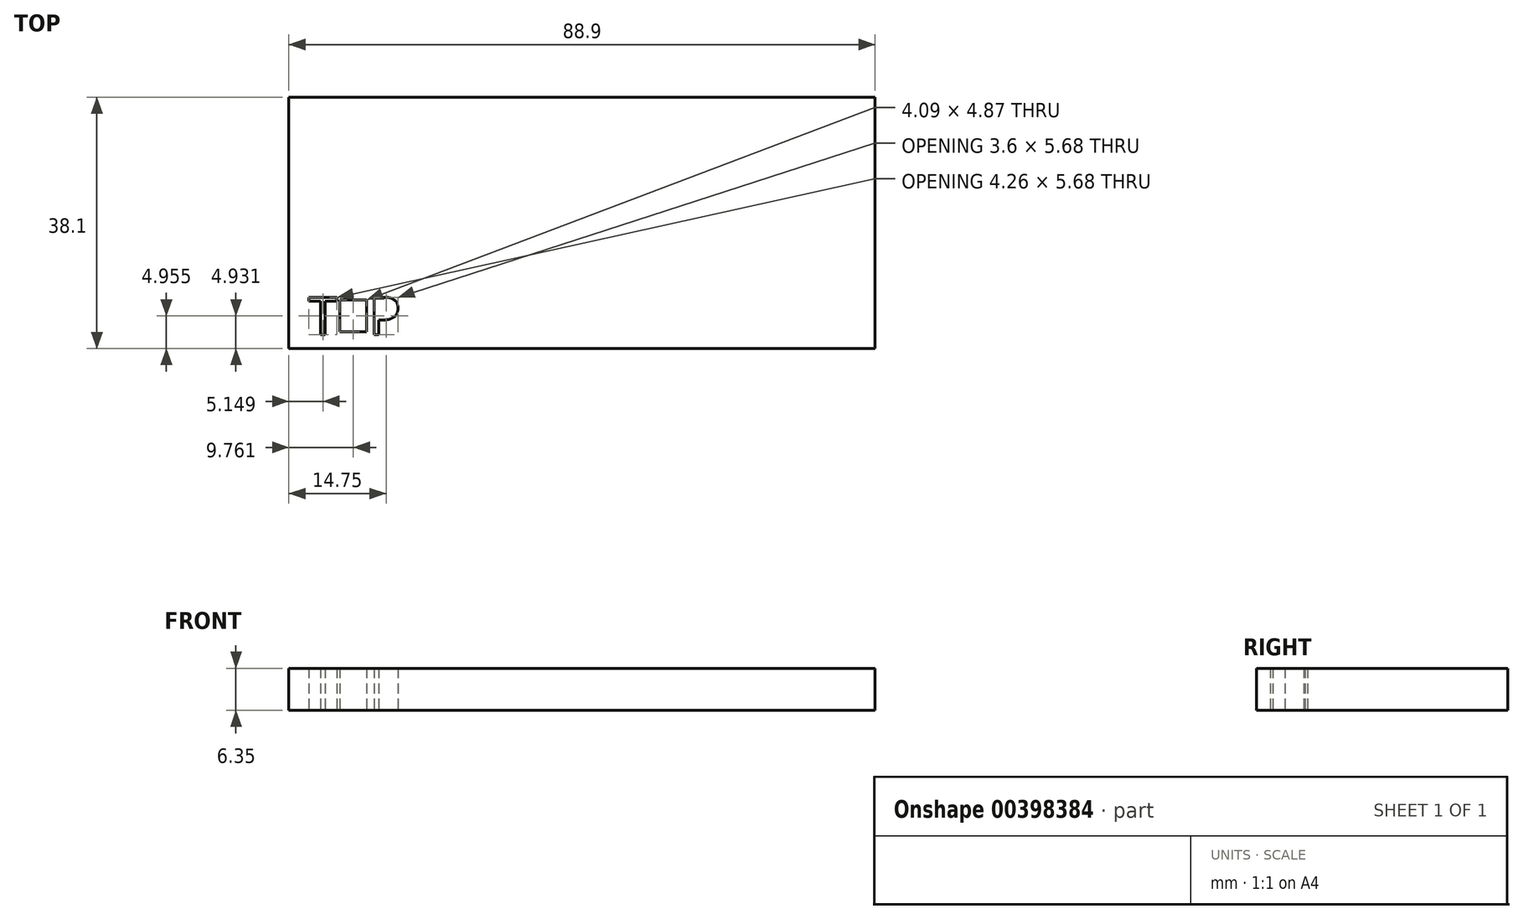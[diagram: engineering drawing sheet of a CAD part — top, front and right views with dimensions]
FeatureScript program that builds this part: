
annotation { "Feature Type Name" : "Feature", "Feature Type Description" : "" }
export const myFeature = defineFeature(function(context is Context, id is Id, definition is map)
    precondition{}
    {
        {
            var Q0;
            Q0=qCreatedBy(makeId("Top.planeOp"),FACE);
            var sketch = newSketch(context, id + "F0", { "sketchPlane" : qUnion([Q0])});
            skLineSegment(sketch, "E0.bottom", {"start": v(-44.45, -19.05) * mm, "end": v(44.45, -19.05) * mm});
            skLineSegment(sketch, "E0.top", {"start": v(-44.45, 19.05) * mm, "end": v(44.45, 19.05) * mm});
            skLineSegment(sketch, "E0.left", {"start": v(-44.45, -19.05) * mm, "end": v(-44.45, 19.05) * mm});
            skLineSegment(sketch, "E0.right", {"start": v(44.45, -19.05) * mm, "end": v(44.45, 19.05) * mm});
            skPoint(sketch, "E0.middle", {"position": v(0, 0) * mm});
            skLineSegment(sketch, "E1", {"start": v(-13.07, 8.02) * mm, "end": v(-13.07, -12.6) * mm});
            skLineSegment(sketch, "E2", {"start": v(-7.34, 0) * mm, "end": v(2.98, 0) * mm});
            skLineSegment(sketch, "E3", {"start": v(13.98, 8.48) * mm, "end": v(4.59, -13.53) * mm});
            skText(sketch, "E4", { "text": "T🚫P", "fontName": "OpenSans-Regular.ttf"});
            const initialGuessF0  = {"E4": [-0.0415, -0.01696, 1, 0, 0.00573]};
            skSetInitialGuess(sketch, initialGuessF0);
            skSolve(sketch);
        }
        {
            var Q0;
            Q0=makeQuery(id+"F0.imprint","IMPRINT",FACE,{"disambiguationData":[TD([[makeQuery(id+"F0.imprint","IMPRINT",EDGE,{"derivedFrom":sQuery(id+"F0.wireOp",EDGE,"E0.bottom")}),1.0]])]});
            extrude(context, id + "F1", {"entities" : qUnion([Q0]), "depth" : 6.35 * mm});
        }
    });
